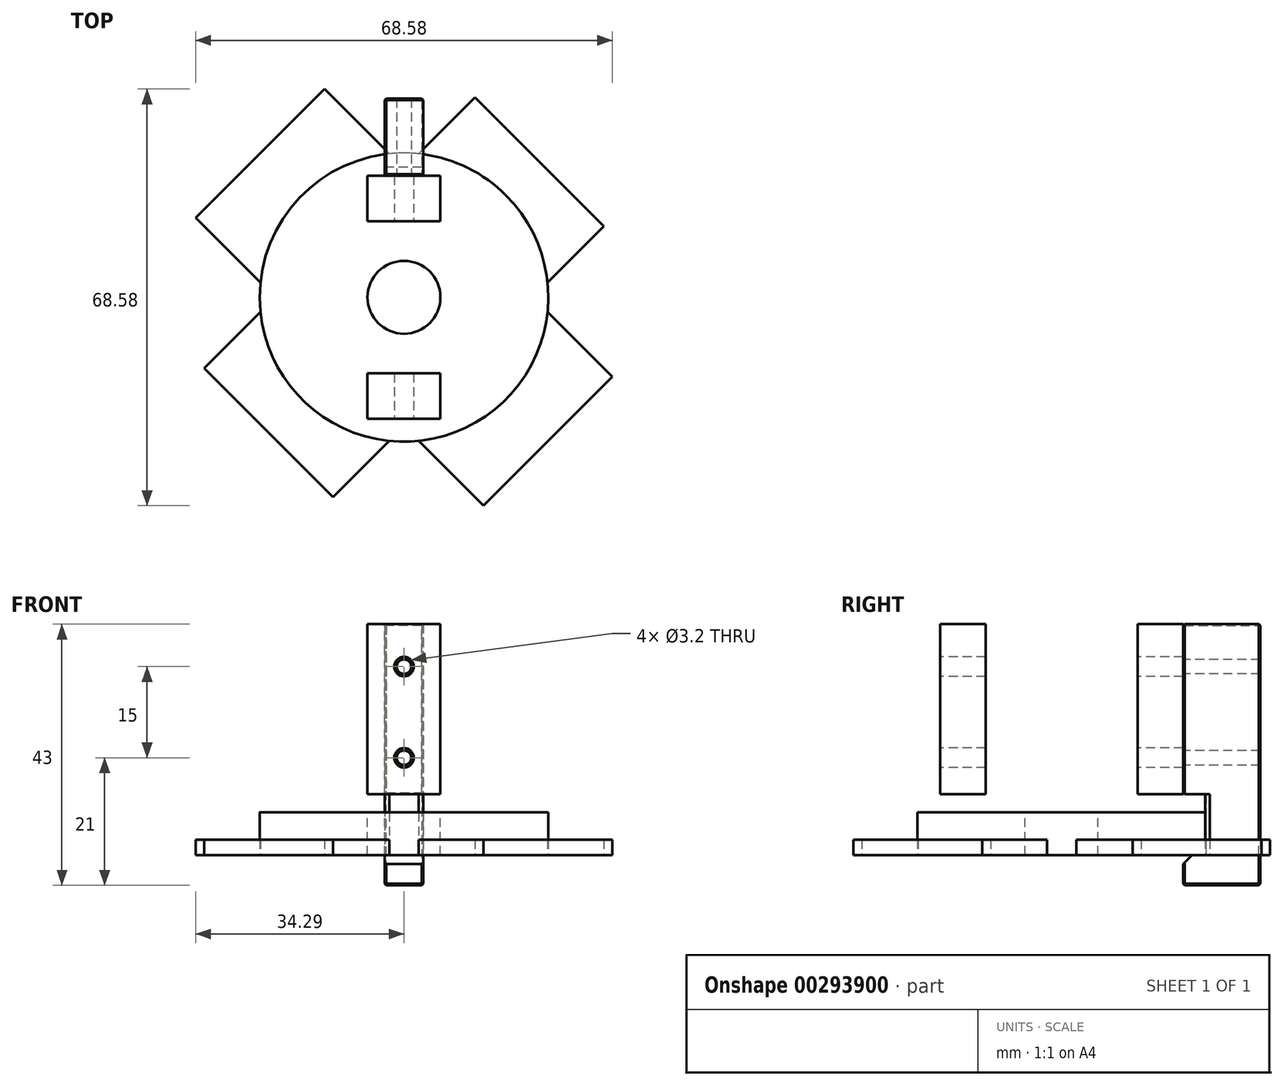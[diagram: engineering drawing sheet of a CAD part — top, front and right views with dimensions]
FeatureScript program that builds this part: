
annotation { "Feature Type Name" : "Feature", "Feature Type Description" : "" }
export const myFeature = defineFeature(function(context is Context, id is Id, definition is map)
    precondition{}
    {
        {
            var Q0;
            Q0=qCreatedBy(makeId("Top.planeOp"),FACE);
            var sketch = newSketch(context, id + "F0", { "sketchPlane" : qUnion([Q0])});
            skCircle(sketch, "E0", {"center": v(0, 0) * mm, "radius": 23.75 * mm});
            skSolve(sketch);
        }
        {
            var Q0;
            Q0 = qSketchRegion(id + "F0", true);
            extrude(context, id + "F1", {"entities" : qUnion([Q0]), "depth" : 7 * mm});
        }
        {
            var Q0;
            Q0=qCreatedBy(makeId("Top.planeOp"),FACE);
            var sketch = newSketch(context, id + "F2", { "sketchPlane" : qUnion([Q0])});
            skLineSegment(sketch, "E1.bottom", {"start": v(31.5, 15) * mm, "end": v(-31.5, 15) * mm});
            skLineSegment(sketch, "E1.top", {"start": v(31.5, -15) * mm, "end": v(-31.5, -15) * mm});
            skLineSegment(sketch, "E1.left", {"start": v(31.5, 15) * mm, "end": v(31.5, -15) * mm});
            skLineSegment(sketch, "E1.right", {"start": v(-31.5, 15) * mm, "end": v(-31.5, -15) * mm});
            skPoint(sketch, "E1.middle", {"position": v(0, 0) * mm});
            skLineSegment(sketch, "E2.bottom", {"start": v(15, 33.5) * mm, "end": v(-15, 33.5) * mm});
            skLineSegment(sketch, "E2.top", {"start": v(15, -33.5) * mm, "end": v(-15, -33.5) * mm});
            skLineSegment(sketch, "E2.left", {"start": v(15, 33.5) * mm, "end": v(15, -33.5) * mm});
            skLineSegment(sketch, "E2.right", {"start": v(-15, 33.5) * mm, "end": v(-15, -33.5) * mm});
            skSolve(sketch);
        }
        {
            var Q0;
            Q0 = qSketchRegion(id + "F2", true);
            extrude(context, id + "F3", {"entities" : qUnion([Q0]), "operationType" : NewBodyOperationType.ADD, "depth" : 2.5 * mm});
        }
        {
            var Q0;
            Q0=makeQuery(id+"F1.opExtrude","CAP_FACE",FACE,{"disambiguationData":[OSD([sQuery(id+"F0.wireOp",EDGE,"E0")])],"isStart":false});
            var sketch = newSketch(context, id + "F4", { "sketchPlane" : qUnion([Q0])});
            skPoint(sketch, "E3", {"position": v(0, 0) * mm});
            skSolve(sketch);
        }
        {
            var Q0;
            Q0=sQuery(id+"F4.wireOp",VERTEX,"E3");
            var Q1;
            Q1=makeQuery(id+"F1.opExtrude","SWEPT_BODY",BODY,{"disambiguationData":[OSD([sQuery(id+"F0.wireOp",EDGE,"E0")])]});
            hole(context, id + "F5", {"style" : HoleStyle.C_BORE, "endStyle" : HoleEndStyle.THROUGH, "standardTappedOrClearance" : lookupTablePath({ "standard" : "ISO", "size" : "12", "type" : "Drilled" }), "standardBlindInLast" : lookupTablePath({ "standard" : "ISO", "size" : "12", "type" : "Drilled" }), "holeDiameter" : 12 * mm, "cBoreDiameter" : 12 * mm, "cBoreDepth" : 5 * mm, "tappedDepth" : 12 * mm, "tapClearance" : 3, "startFromSketch" : true, "locations" : qUnion([Q0]), "scope" : qUnion([Q1])});
        }
        {
            var Q0;
            Q0=qCreatedBy(makeId("Top.planeOp"),FACE);
            cPlane(context, id + "F6", {"entities" : qUnion([Q0]), "cplaneType" : CPlaneType.OFFSET, "offset" : 10 * mm, "width" : 150 * mm, "height" : 150 * mm});
        }
        {
            var Q0;
            Q0=qCreatedBy(id+"F6.planeOp",FACE);
            var sketch = newSketch(context, id + "F7", { "sketchPlane" : qUnion([Q0])});
            skLineSegment(sketch, "E4.bottom", {"start": v(20, 6) * mm, "end": v(-20, 6) * mm});
            skLineSegment(sketch, "E4.top", {"start": v(20, -6) * mm, "end": v(-20, -6) * mm});
            skLineSegment(sketch, "E4.left", {"start": v(20, 6) * mm, "end": v(20, -6) * mm});
            skLineSegment(sketch, "E4.right", {"start": v(-20, 6) * mm, "end": v(-20, -6) * mm});
            skPoint(sketch, "E4.middle", {"position": v(0, 0) * mm});
            skSolve(sketch);
        }
        {
            var Q0;
            Q0 = qSketchRegion(id + "F7", true);
            extrude(context, id + "F8", {"entities" : qUnion([Q0]), "depth" : 28 * mm});
        }
        {
            var Q0;
            Q0=qCreatedBy(makeId("Front.planeOp"),FACE);
            var sketch = newSketch(context, id + "F9", { "sketchPlane" : qUnion([Q0])});
            skLineSegment(sketch, "E5", {"start": v(0, -46.12) * mm, "end": v(0, 77.52) * mm, "construction": true});
            skSolve(sketch);
        }
        {
            var Q0;
            Q0=makeQuery(id+"F8.opExtrude","SWEPT_BODY",BODY,{"disambiguationData":[OSD([sQuery(id+"F7.wireOp",EDGE,"E4.bottom"),sQuery(id+"F7.wireOp",EDGE,"E4.top"),sQuery(id+"F7.wireOp",EDGE,"E4.left"),sQuery(id+"F7.wireOp",EDGE,"E4.right")])]});
            var Q1;
            Q1=sQuery(id+"F9.wireOp",EDGE,"E5");
            transform(context, id + "F10", {"entities" : qUnion([Q0]), "transformType" : TransformType.ROTATION, "transformAxis" : qUnion([Q1]), "angle" : 45 * degree, "makeCopy" : false});
        }
        {
            var Q0;
            Q0=makeQuery(id+"F8.opExtrude","SWEPT_FACE",FACE,{"disambiguationData":[OSD([sQuery(id+"F7.wireOp",EDGE,"E4.right")])]});
            var sketch = newSketch(context, id + "F11", { "sketchPlane" : qUnion([Q0])});
            skPoint(sketch, "E6", {"position": v(0, 31) * mm});
            skPoint(sketch, "E6.positionSnap0", {"position": v(0, 38) * mm});
            skPoint(sketch, "E7", {"position": v(0, 16) * mm});
            skSolve(sketch);
        }
        {
            var Q0;
            Q0=sQuery(id+"F11.wireOp",VERTEX,"E6");
            var Q1;
            Q1=sQuery(id+"F11.wireOp",VERTEX,"E7");
            var Q2;
            Q2=makeQuery(id+"F8.opExtrude","SWEPT_BODY",BODY,{"disambiguationData":[OSD([sQuery(id+"F7.wireOp",EDGE,"E4.bottom"),sQuery(id+"F7.wireOp",EDGE,"E4.top"),sQuery(id+"F7.wireOp",EDGE,"E4.left"),sQuery(id+"F7.wireOp",EDGE,"E4.right")])]});
            hole(context, id + "F12", {"style" : HoleStyle.SIMPLE, "endStyle" : HoleEndStyle.THROUGH, "standardTappedOrClearance" : lookupTablePath({ "standard" : "ISO", "engagement" : "75%", "pitch" : "0.75 mm", "size" : "M4", "type" : "Tapped" }), "standardBlindInLast" : lookupTablePath({ "standard" : "ISO", "engagement" : "75%", "pitch" : "0.75 mm", "size" : "M4", "type" : "Tapped" }), "holeDiameter" : 3.2 * mm, "showTappedDepth" : true, "tappedDepth" : 12 * mm, "tapClearance" : 3, "startFromSketch" : true, "locations" : qUnion([Q0, Q1]), "scope" : qUnion([Q2])});
        }
        {
            var Q0;
            Q0=makeQuery(id+"F8.opExtrude","CAP_FACE",FACE,{"disambiguationData":[OSD([sQuery(id+"F7.wireOp",EDGE,"E4.bottom"),sQuery(id+"F7.wireOp",EDGE,"E4.top"),sQuery(id+"F7.wireOp",EDGE,"E4.left"),sQuery(id+"F7.wireOp",EDGE,"E4.right")])],"isStart":false});
            var sketch = newSketch(context, id + "F13", { "sketchPlane" : qUnion([Q0])});
            skLineSegment(sketch, "E8.0", {"start": v(9.9, 18.38) * mm, "end": v(-18.38, -9.9) * mm});
            skLineSegment(sketch, "E9.0", {"start": v(9.9, 18.38) * mm, "end": v(18.38, 9.9) * mm});
            skLineSegment(sketch, "E10.0", {"start": v(-18.38, -9.9) * mm, "end": v(-9.9, -18.38) * mm});
            skLineSegment(sketch, "E11.0", {"start": v(-13.08, -4.6) * mm, "end": v(-4.6, -13.08) * mm});
            skLineSegment(sketch, "E12.0", {"start": v(4.6, 13.08) * mm, "end": v(13.08, 4.6) * mm});
            skSolve(sketch);
        }
        {
            var Q0;
            {var subQ0=sQuery(id+"F13.wireOp",EDGE,"E11.0");Q0=makeQuery(id+"F13.imprint","IMPRINT",FACE,{"disambiguationData":[TD([[makeQuery(id+"F13.imprint","IMPRINT",EDGE,{"derivedFrom":subQ0}),1.0]])]});}
            var Q1;
            Q1=makeQuery(id+"F8.opExtrude","CAP_FACE",FACE,{"disambiguationData":[OSD([sQuery(id+"F7.wireOp",EDGE,"E4.bottom"),sQuery(id+"F7.wireOp",EDGE,"E4.top"),sQuery(id+"F7.wireOp",EDGE,"E4.left"),sQuery(id+"F7.wireOp",EDGE,"E4.right")])],"isStart":true});
            extrude(context, id + "F14", {"entities" : qUnion([Q0]), "operationType" : NewBodyOperationType.REMOVE, "endBound" : BoundingType.UP_TO_SURFACE, "oppositeDirection" : true, "endBoundEntityFace" : qUnion([Q1]), "depth" : 25 * mm});
        }
        {
            var Q0;
            Q0=makeQuery(id+"F1.opExtrude","SWEPT_BODY",BODY,{"disambiguationData":[OSD([sQuery(id+"F0.wireOp",EDGE,"E0")])]});
            var Q1;
            Q1=makeQuery(id+"F14.boolean.opBoolean","SPLIT",BODY,{"disambiguationData":[OD(1.0)],"derivedFrom":makeQuery(id+"F8.opExtrude","SWEPT_BODY",BODY,{"disambiguationData":[OSD([sQuery(id+"F7.wireOp",EDGE,"E4.bottom"),sQuery(id+"F7.wireOp",EDGE,"E4.top"),sQuery(id+"F7.wireOp",EDGE,"E4.left"),sQuery(id+"F7.wireOp",EDGE,"E4.right")])]})});
            var Q2;
            Q2=makeQuery(id+"F14.boolean.opBoolean","SPLIT",BODY,{"disambiguationData":[OD(0.0)],"derivedFrom":makeQuery(id+"F8.opExtrude","SWEPT_BODY",BODY,{"disambiguationData":[OSD([sQuery(id+"F7.wireOp",EDGE,"E4.bottom"),sQuery(id+"F7.wireOp",EDGE,"E4.top"),sQuery(id+"F7.wireOp",EDGE,"E4.left"),sQuery(id+"F7.wireOp",EDGE,"E4.right")])]})});
            var Q3;
            Q3=sQuery(id+"F9.wireOp",EDGE,"E5");
            transform(context, id + "F15", {"entities" : qUnion([Q0, Q1, Q2]), "transformType" : TransformType.ROTATION, "transformAxis" : qUnion([Q3]), "angle" : 45 * degree, "makeCopy" : false});
        }
        {
            var Q0;
            Q0=qCreatedBy(makeId("Right.planeOp"),FACE);
            var sketch = newSketch(context, id + "F16", { "sketchPlane" : qUnion([Q0])});
            skPoint(sketch, "E13.0", {"position": v(20, 38) * mm});
            skLineSegment(sketch, "E14.bottom", {"start": v(20, 38) * mm, "end": v(32.7, 38) * mm});
            skLineSegment(sketch, "E14.top", {"start": v(20, -2) * mm, "end": v(32.7, -2) * mm});
            skLineSegment(sketch, "E14.left", {"start": v(20, 38) * mm, "end": v(20, -2) * mm});
            skLineSegment(sketch, "E14.right", {"start": v(32.7, 38) * mm, "end": v(32.7, -2) * mm});
            skSolve(sketch);
        }
        {
            var Q0;
            Q0=makeQuery(id+"F16.imprint","IMPRINT",FACE,{"disambiguationData":[TD([[makeQuery(id+"F16.imprint","IMPRINT",EDGE,{"derivedFrom":sQuery(id+"F16.wireOp",EDGE,"E14.bottom")}),-1.0]])]});
            extrude(context, id + "F17", {"entities" : qUnion([Q0]), "endBound" : BoundingType.SYMMETRIC, "depth" : 6.35 * mm});
        }
        {
            var Q0;
            Q0=makeQuery(id+"F1.opExtrude","SWEPT_BODY",BODY,{"disambiguationData":[OSD([sQuery(id+"F0.wireOp",EDGE,"E0")])]});
            var Q1;
            Q1=makeQuery(id+"F17.opExtrude","SWEPT_BODY",BODY,{"disambiguationData":[OSD([sQuery(id+"F16.wireOp",EDGE,"E14.bottom"),sQuery(id+"F16.wireOp",EDGE,"E14.top"),sQuery(id+"F16.wireOp",EDGE,"E14.left"),sQuery(id+"F16.wireOp",EDGE,"E14.right")])]});
            booleanBodies(context, id + "F18", {"operationType" : BooleanOperationType.SUBTRACTION, "tools" : qUnion([Q0]), "targets" : qUnion([Q1]), "keepTools" : true});
        }
        {
            var Q0;
            Q0=makeQuery(id+"F18.opBoolean","INTERSECT",EDGE,{"derivedFrom":[makeQuery(id+"F3.boolean.opBoolean","MERGE",FACE,{"derivedFrom":[makeQuery(id+"F1.opExtrude","CAP_FACE",FACE,{"disambiguationData":[OSD([sQuery(id+"F0.wireOp",EDGE,"E0")])],"isStart":true}),makeQuery(id+"F3.opExtrude","CAP_FACE",FACE,{"disambiguationData":[OSD([sQuery(id+"F2.wireOp",EDGE,"E1.bottom"),sQuery(id+"F2.wireOp",EDGE,"E1.top"),sQuery(id+"F2.wireOp",EDGE,"E1.left"),sQuery(id+"F2.wireOp",EDGE,"E1.right"),sQuery(id+"F2.wireOp",EDGE,"E2.bottom"),sQuery(id+"F2.wireOp",EDGE,"E2.top"),sQuery(id+"F2.wireOp",EDGE,"E2.left"),sQuery(id+"F2.wireOp",EDGE,"E2.right")])],"isStart":true})]}),makeQuery(id+"F17.opExtrude","SWEPT_FACE",FACE,{"disambiguationData":[OSD([sQuery(id+"F16.wireOp",EDGE,"E14.left")])]})]});
            chamfer(context, id + "F19", {"entities" : qUnion([Q0]), "width" : 1.5 * mm, "tangentPropagation" : true});
        }
        {
            var Q0;
            {var subQ0=sQuery(id+"F2.wireOp",EDGE,"E1.left");var subQ1=sQuery(id+"F2.wireOp",EDGE,"E1.bottom");var subQ2=sQuery(id+"F2.wireOp",EDGE,"E2.left");var subQ3=sQuery(id+"F2.wireOp",EDGE,"E1.top");Q0=makeQuery(id+"F18.opBoolean","COPY",FACE,{"derivedFrom":makeQuery(id+"F3.boolean.opBoolean","SPLIT",FACE,{"disambiguationData":[TD([makeQuery(id+"F3.opExtrude","SWEPT_FACE",FACE,{"disambiguationData":[OSD([subQ0])]})])],"derivedFrom":makeQuery(id+"F3.opExtrude","CAP_FACE",FACE,{"disambiguationData":[OSD([subQ1,subQ3,subQ0,sQuery(id+"F2.wireOp",EDGE,"E1.right"),sQuery(id+"F2.wireOp",EDGE,"E2.bottom"),sQuery(id+"F2.wireOp",EDGE,"E2.top"),subQ2,sQuery(id+"F2.wireOp",EDGE,"E2.right")])],"isStart":false})})});}
            var Q1;
            Q1=makeQuery(id+"F18.opBoolean","COPY",FACE,{"derivedFrom":makeQuery(id+"F1.opExtrude","CAP_FACE",FACE,{"disambiguationData":[OSD([sQuery(id+"F0.wireOp",EDGE,"E0")])],"isStart":false})});
            extrude(context, id + "F20", {"entities" : qUnion([Q0]), "operationType" : NewBodyOperationType.REMOVE, "endBound" : BoundingType.UP_TO_SURFACE, "oppositeDirection" : true, "endBoundEntityFace" : qUnion([Q1]), "depth" : 25 * mm});
        }
        {
            var Q0;
            {var subQ0=sQuery(id+"F2.wireOp",EDGE,"E2.right");var subQ1=sQuery(id+"F2.wireOp",EDGE,"E2.bottom");var subQ2=sQuery(id+"F2.wireOp",EDGE,"E1.bottom");var subQ3=sQuery(id+"F2.wireOp",EDGE,"E2.left");Q0=makeQuery(id+"F18.opBoolean","COPY",FACE,{"derivedFrom":makeQuery(id+"F3.boolean.opBoolean","SPLIT",FACE,{"disambiguationData":[TD([makeQuery(id+"F3.opExtrude","SWEPT_FACE",FACE,{"disambiguationData":[OSD([subQ1])]})])],"derivedFrom":makeQuery(id+"F3.opExtrude","CAP_FACE",FACE,{"disambiguationData":[OSD([subQ2,sQuery(id+"F2.wireOp",EDGE,"E1.top"),sQuery(id+"F2.wireOp",EDGE,"E1.left"),sQuery(id+"F2.wireOp",EDGE,"E1.right"),subQ1,sQuery(id+"F2.wireOp",EDGE,"E2.top"),subQ3,subQ0])],"isStart":false})})});}
            var Q1;
            {var subQ0=sQuery(id+"F0.wireOp",EDGE,"E0");Q1=makeQuery(id+"F20.boolean.opBoolean","MERGE",FACE,{"derivedFrom":[makeQuery(id+"F18.opBoolean","COPY",FACE,{"derivedFrom":makeQuery(id+"F1.opExtrude","CAP_FACE",FACE,{"disambiguationData":[OSD([subQ0])],"isStart":false})}),makeQuery(id+"F20.opExtrude","CAP_FACE",FACE,{"disambiguationData":[OSD([subQ0])],"isStart":false})]});}
            extrude(context, id + "F21", {"entities" : qUnion([Q0]), "operationType" : NewBodyOperationType.REMOVE, "endBound" : BoundingType.UP_TO_SURFACE, "oppositeDirection" : true, "endBoundEntityFace" : qUnion([Q1]), "depth" : 25 * mm});
        }
        {
            var Q0;
            {var subQ2=sQuery(id+"F16.wireOp",EDGE,"E14.left");Q0=makeQuery(id+"F18.opBoolean","SPLIT",FACE,{"disambiguationData":[TD([makeQuery(id+"F1.opExtrude","CAP_FACE",FACE,{"disambiguationData":[OSD([sQuery(id+"F0.wireOp",EDGE,"E0")])],"isStart":false})])],"derivedFrom":makeQuery(id+"F17.opExtrude","SWEPT_FACE",FACE,{"disambiguationData":[OSD([subQ2])]})});}
            var sketch = newSketch(context, id + "F22", { "sketchPlane" : qUnion([Q0])});
            skPoint(sketch, "E15", {"position": v(0, 16) * mm});
            skPoint(sketch, "E16", {"position": v(0, 31) * mm});
            skSolve(sketch);
        }
        {
            var Q0;
            Q0=sQuery(id+"F22.wireOp",VERTEX,"E16");
            var Q1;
            Q1=sQuery(id+"F22.wireOp",VERTEX,"E15");
            var Q2;
            Q2=makeQuery(id+"F17.opExtrude","SWEPT_BODY",BODY,{"disambiguationData":[OSD([sQuery(id+"F16.wireOp",EDGE,"E14.bottom"),sQuery(id+"F16.wireOp",EDGE,"E14.top"),sQuery(id+"F16.wireOp",EDGE,"E14.left"),sQuery(id+"F16.wireOp",EDGE,"E14.right")])]});
            hole(context, id + "F23", {"style" : HoleStyle.SIMPLE, "endStyle" : HoleEndStyle.THROUGH, "standardTappedOrClearance" : lookupTablePath({ "standard" : "ISO", "engagement" : "75%", "pitch" : "0.6 mm", "size" : "M3", "type" : "Tapped" }), "standardBlindInLast" : lookupTablePath({ "standard" : "ISO", "engagement" : "75%", "pitch" : "0.6 mm", "size" : "M3", "type" : "Tapped" }), "holeDiameter" : 2.4 * mm, "showTappedDepth" : true, "tappedDepth" : 12 * mm, "tapClearance" : 3, "startFromSketch" : true, "locations" : qUnion([Q0, Q1]), "scope" : qUnion([Q2])});
        }
        {
            var Q0;
            {var subQ0=sQuery(id+"F0.wireOp",EDGE,"E0");Q0=makeQuery(id+"F21.boolean.opBoolean","MERGE",FACE,{"derivedFrom":[makeQuery(id+"F20.boolean.opBoolean","MERGE",FACE,{"derivedFrom":[makeQuery(id+"F18.opBoolean","COPY",FACE,{"derivedFrom":makeQuery(id+"F1.opExtrude","CAP_FACE",FACE,{"disambiguationData":[OSD([subQ0])],"isStart":false})}),makeQuery(id+"F20.opExtrude","CAP_FACE",FACE,{"disambiguationData":[OSD([subQ0])],"isStart":false})]}),makeQuery(id+"F21.opExtrude","CAP_FACE",FACE,{"disambiguationData":[OSD([subQ0])],"isStart":false})]});}
            var Q1;
            {var subQ0=sQuery(id+"F7.wireOp",EDGE,"E4.bottom");var subQ1=sQuery(id+"F7.wireOp",EDGE,"E4.top");var subQ2=sQuery(id+"F7.wireOp",EDGE,"E4.left");Q1=makeQuery(id+"F14.boolean.opBoolean","SPLIT",FACE,{"disambiguationData":[TD([makeQuery(id+"F8.opExtrude","SWEPT_FACE",FACE,{"disambiguationData":[OSD([subQ2])]})])],"derivedFrom":makeQuery(id+"F8.opExtrude","CAP_FACE",FACE,{"disambiguationData":[OSD([subQ0,subQ1,subQ2,sQuery(id+"F7.wireOp",EDGE,"E4.right")])],"isStart":true})});}
            var Q2;
            Q2=makeQuery(id+"F14.boolean.opBoolean","SPLIT",BODY,{"disambiguationData":[OD(0.0)],"derivedFrom":makeQuery(id+"F8.opExtrude","SWEPT_BODY",BODY,{"disambiguationData":[OSD([sQuery(id+"F7.wireOp",EDGE,"E4.bottom"),sQuery(id+"F7.wireOp",EDGE,"E4.top"),sQuery(id+"F7.wireOp",EDGE,"E4.left"),sQuery(id+"F7.wireOp",EDGE,"E4.right")])]})});
            extrude(context, id + "F24", {"entities" : qUnion([Q0]), "operationType" : NewBodyOperationType.REMOVE, "endBound" : BoundingType.UP_TO_SURFACE, "oppositeDirection" : true, "endBoundEntityFace" : qUnion([Q1]), "endBoundEntityBody" : qUnion([Q2]), "depth" : 25 * mm});
        }
        {
            var Q0;
            Q0=makeQuery(id+"F17.opExtrude","SWEPT_FACE",FACE,{"disambiguationData":[OSD([sQuery(id+"F16.wireOp",EDGE,"E14.top")])]});
            extrude(context, id + "F25", {"entities" : qUnion([Q0]), "operationType" : NewBodyOperationType.ADD, "depth" : 3 * mm});
        }
        {
            var Q0;
            {var subQ0=sQuery(id+"F16.wireOp",EDGE,"E14.right");var subQ1=sQuery(id+"F16.wireOp",EDGE,"E14.top");Q0=makeQuery(id+"F25.boolean.opBoolean","MERGE",EDGE,{"derivedFrom":[makeQuery(id+"F17.opExtrude","CAP_EDGE",EDGE,{"disambiguationData":[OSD([subQ0])],"isStart":false}),makeQuery(id+"F25.opExtrude","SWEPT_EDGE",EDGE,{"disambiguationData":[OSD([subQ1,subQ0]),TDD([makeQuery(id+"F17.opExtrude","CAP_VERTEX",VERTEX,{"disambiguationData":[OSD([subQ1,subQ0])],"isStart":false})])]})]});}
            var Q1;
            {var subQ2=sQuery(id+"F16.wireOp",EDGE,"E14.left");Q1=makeQuery(id+"F18.opBoolean","SPLIT",FACE,{"disambiguationData":[TD([makeQuery(id+"F1.opExtrude","CAP_FACE",FACE,{"disambiguationData":[OSD([sQuery(id+"F0.wireOp",EDGE,"E0")])],"isStart":false})])],"derivedFrom":makeQuery(id+"F17.opExtrude","SWEPT_FACE",FACE,{"disambiguationData":[OSD([subQ2])]})});}
            var Q2;
            {var subQ0=sQuery(id+"F16.wireOp",EDGE,"E14.right");var subQ1=sQuery(id+"F16.wireOp",EDGE,"E14.top");Q2=makeQuery(id+"F25.boolean.opBoolean","MERGE",EDGE,{"derivedFrom":[makeQuery(id+"F17.opExtrude","CAP_EDGE",EDGE,{"disambiguationData":[OSD([subQ0])],"isStart":true}),makeQuery(id+"F25.opExtrude","SWEPT_EDGE",EDGE,{"disambiguationData":[OSD([subQ1,subQ0]),TDD([makeQuery(id+"F17.opExtrude","CAP_VERTEX",VERTEX,{"disambiguationData":[OSD([subQ1,subQ0])],"isStart":true})])]})]});}
            var Q3;
            Q3=makeQuery(id+"F17.opExtrude","SWEPT_EDGE",EDGE,{"disambiguationData":[OSD([sQuery(id+"F16.wireOp",EDGE,"E14.bottom"),sQuery(id+"F16.wireOp",EDGE,"E14.right")])]});
            var Q4;
            Q4=makeQuery(id+"F17.opExtrude","CAP_EDGE",EDGE,{"disambiguationData":[OSD([sQuery(id+"F16.wireOp",EDGE,"E14.bottom")])],"isStart":true});
            var Q5;
            Q5=makeQuery(id+"F23.hole-1.boolean.opBoolean","INTERSECT",EDGE,{"derivedFrom":[makeQuery(id+"F17.opExtrude","SWEPT_FACE",FACE,{"disambiguationData":[OSD([sQuery(id+"F16.wireOp",EDGE,"E14.right")])]}),makeQuery(id+"F23.hole-1.opRevolve","SWEPT_FACE",FACE,{"disambiguationData":[OSD([sQuery(id+"F23.hole-1.sketch.wireOp",EDGE,"core_line_2")])]})]});
            var Q6;
            Q6=makeQuery(id+"F23.hole-0.boolean.opBoolean","INTERSECT",EDGE,{"derivedFrom":[makeQuery(id+"F17.opExtrude","SWEPT_FACE",FACE,{"disambiguationData":[OSD([sQuery(id+"F16.wireOp",EDGE,"E14.right")])]}),makeQuery(id+"F23.hole-0.opRevolve","SWEPT_FACE",FACE,{"disambiguationData":[OSD([sQuery(id+"F23.hole-0.sketch.wireOp",EDGE,"core_line_2")])]})]});
            var Q7;
            Q7=makeQuery(id+"F25.opExtrude","CAP_FACE",FACE,{"disambiguationData":[OSD([sQuery(id+"F16.wireOp",EDGE,"E14.top")])],"isStart":false});
            var Q8;
            {var subQ0=sQuery(id+"F16.wireOp",EDGE,"E14.left");var subQ1=sQuery(id+"F16.wireOp",EDGE,"E14.top");Q8=makeQuery(id+"F25.boolean.opBoolean","MERGE",EDGE,{"derivedFrom":[makeQuery(id+"F18.opBoolean","SPLIT",EDGE,{"disambiguationData":[TD([makeQuery(id+"F1.opExtrude","CAP_FACE",FACE,{"disambiguationData":[OSD([sQuery(id+"F0.wireOp",EDGE,"E0")])],"isStart":true})])],"derivedFrom":makeQuery(id+"F17.opExtrude","CAP_EDGE",EDGE,{"disambiguationData":[OSD([subQ0])],"isStart":true})}),makeQuery(id+"F25.opExtrude","SWEPT_EDGE",EDGE,{"disambiguationData":[OSD([subQ1,subQ0]),TDD([makeQuery(id+"F17.opExtrude","CAP_VERTEX",VERTEX,{"disambiguationData":[OSD([subQ1,subQ0])],"isStart":true})])]})]});}
            var Q9;
            {var subQ0=sQuery(id+"F16.wireOp",EDGE,"E14.left");var subQ1=sQuery(id+"F16.wireOp",EDGE,"E14.top");Q9=makeQuery(id+"F25.boolean.opBoolean","MERGE",EDGE,{"derivedFrom":[makeQuery(id+"F18.opBoolean","SPLIT",EDGE,{"disambiguationData":[TD([makeQuery(id+"F1.opExtrude","CAP_FACE",FACE,{"disambiguationData":[OSD([sQuery(id+"F0.wireOp",EDGE,"E0")])],"isStart":true})])],"derivedFrom":makeQuery(id+"F17.opExtrude","CAP_EDGE",EDGE,{"disambiguationData":[OSD([subQ0])],"isStart":false})}),makeQuery(id+"F25.opExtrude","SWEPT_EDGE",EDGE,{"disambiguationData":[OSD([subQ1,subQ0]),TDD([makeQuery(id+"F17.opExtrude","CAP_VERTEX",VERTEX,{"disambiguationData":[OSD([subQ1,subQ0])],"isStart":false})])]})]});}
            chamfer(context, id + "F26", {"entities" : qUnion([Q0, Q1, Q2, Q3, Q4, Q5, Q6, Q7, Q8, Q9]), "width" : .25 * mm, "tangentPropagation" : true});
        }
    });
